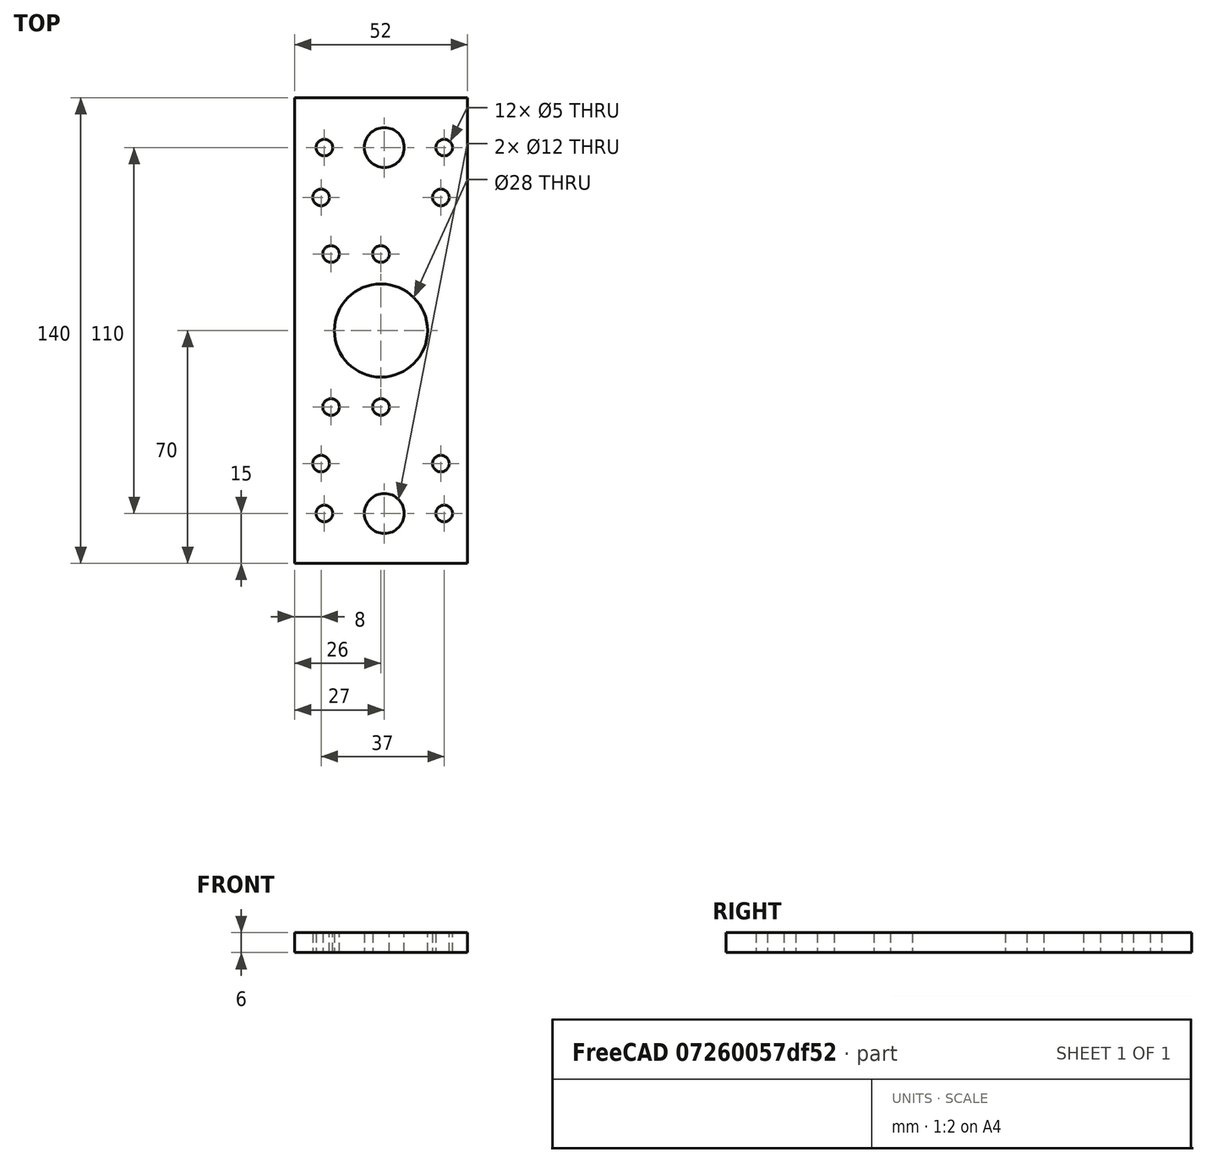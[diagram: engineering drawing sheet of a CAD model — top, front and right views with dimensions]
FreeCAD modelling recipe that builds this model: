
FCSTD DOCUMENT  (FreeCAD 0.15R4671 (Git))
Label: top
License: All rights reserved
LicenseURL: http://en.wikipedia.org/wiki/All_rights_reserved
objects: Drawing::FeatureView×25, Drawing::FeatureViewPart×2, Sketcher::SketchObject×1, PartDesign::Pad×1, Drawing::FeaturePage×1
note: 3 computed .brp shape members not serialized (recipe doc carries the construction recipe); baked Part::Feature solids carry a one-line shape summary decoded from their .brp

FEATURE [Sketcher::SketchObject] Sketch  label="top-sketch"
  sketch-geometry (32):
    g0: LineSegment StartX=-26 StartY=70 StartZ=0 EndX=26 EndY=70 EndZ=0
    g1: LineSegment StartX=26 StartY=70 StartZ=0 EndX=26 EndY=-70 EndZ=0
    g2: LineSegment StartX=26 StartY=-70 StartZ=0 EndX=-26 EndY=-70 EndZ=0
    g3: LineSegment StartX=-26 StartY=-70 StartZ=0 EndX=-26 EndY=70 EndZ=0
    g4: Circle CenterX=0 CenterY=0 CenterZ=0 NormalX=0 NormalY=0 NormalZ=1 Radius=14
    g5: LineSegment [constr] StartX=-15 StartY=23 StartZ=0 EndX=0 EndY=23 EndZ=0
    g6: LineSegment [constr] StartX=0 StartY=23 StartZ=0 EndX=0 EndY=-23 EndZ=0
    g7: LineSegment [constr] StartX=0 StartY=-23 StartZ=0 EndX=-15 EndY=-23 EndZ=0
    g8: LineSegment [constr] StartX=-15 StartY=-23 StartZ=0 EndX=-15 EndY=23 EndZ=0
    g9: Circle CenterX=-15 CenterY=23 CenterZ=0 NormalX=0 NormalY=0 NormalZ=1 Radius=2.5
    g10: Circle CenterX=0 CenterY=23 CenterZ=0 NormalX=0 NormalY=0 NormalZ=1 Radius=2.5
    g11: Circle CenterX=-15 CenterY=-23 CenterZ=0 NormalX=0 NormalY=0 NormalZ=1 Radius=2.5
    g12: Circle CenterX=0 CenterY=-23 CenterZ=0 NormalX=0 NormalY=0 NormalZ=1 Radius=2.5
    g13: LineSegment [constr] StartX=-18 StartY=40 StartZ=0 EndX=18 EndY=40 EndZ=0
    g14: LineSegment [constr] StartX=18 StartY=40 StartZ=0 EndX=18 EndY=-40 EndZ=0
    g15: LineSegment [constr] StartX=18 StartY=-40 StartZ=0 EndX=-18 EndY=-40 EndZ=0
    g16: LineSegment [constr] StartX=-18 StartY=-40 StartZ=0 EndX=-18 EndY=40 EndZ=0
    g17: Circle CenterX=-18 CenterY=40 CenterZ=0 NormalX=0 NormalY=0 NormalZ=1 Radius=2.5
    g18: Circle CenterX=18 CenterY=40 CenterZ=0 NormalX=0 NormalY=0 NormalZ=1 Radius=2.5
    g19: Circle CenterX=18 CenterY=-40 CenterZ=0 NormalX=0 NormalY=0 NormalZ=1 Radius=2.5
    g20: Circle CenterX=-18 CenterY=-40 CenterZ=0 NormalX=0 NormalY=0 NormalZ=1 Radius=2.5
    g21: LineSegment [constr] StartX=-17 StartY=55 StartZ=0 EndX=19 EndY=55 EndZ=0
    g22: LineSegment [constr] StartX=19 StartY=55 StartZ=0 EndX=19 EndY=-55 EndZ=0
    g23: LineSegment [constr] StartX=19 StartY=-55 StartZ=0 EndX=-17 EndY=-55 EndZ=0
    g24: LineSegment [constr] StartX=-17 StartY=-55 StartZ=0 EndX=-17 EndY=55 EndZ=0
    g25: Circle CenterX=1 CenterY=55 CenterZ=0 NormalX=0 NormalY=0 NormalZ=1 Radius=6
    g26: Circle CenterX=1 CenterY=-55 CenterZ=0 NormalX=0 NormalY=0 NormalZ=1 Radius=6
    g27: LineSegment [constr] StartX=1 StartY=55 StartZ=0 EndX=1 EndY=-55 EndZ=0
    g28: Circle CenterX=-17 CenterY=55 CenterZ=0 NormalX=0 NormalY=0 NormalZ=1 Radius=2.5
    g29: Circle CenterX=19 CenterY=55 CenterZ=0 NormalX=0 NormalY=0 NormalZ=1 Radius=2.5
    g30: Circle CenterX=-17 CenterY=-55 CenterZ=0 NormalX=0 NormalY=0 NormalZ=1 Radius=2.5
    g31: Circle CenterX=19 CenterY=-55 CenterZ=0 NormalX=0 NormalY=0 NormalZ=1 Radius=2.5
  constraints (82):
    c: Coincident(g1,g2)
    c: Coincident(g2,g3)
    c: Coincident(g3,g0)
    c: Horizontal(g0)
    c: Horizontal(g2)
    c: Vertical(g1)
    c: Vertical(g3)
    c: Symmetric(g1,g2,g-2)
    c: Symmetric(g0,g1,g-1)
    c: Coincident(g4,g-1)
    c: Radius(g4) = 14
    c: Coincident(g5,g6)
    c: Coincident(g6,g7)
    c: Coincident(g7,g8)
    c: Coincident(g8,g5)
    c: Horizontal(g5)
    c: Horizontal(g7)
    c: Vertical(g6)
    c: Vertical(g8)
    c: PointOnObject(g6,g-2)
    c: Symmetric(g5,g6,g-1)
    c: DistanceY(g5,g7) = -46
    c: DistanceX(g5,g5) = 15
    c: Coincident(g9,g5)
    c: Coincident(g10,g5)
    c: Coincident(g11,g7)
    c: Coincident(g12,g6)
    c: Radius(g12) = 2.5
    c: Equal(g12,g11)
    c: Equal(g12,g9)
    c: Equal(g12,g10)
    c: Coincident(g13,g14)
    c: Coincident(g14,g15)
    c: Coincident(g15,g16)
    c: Coincident(g16,g13)
    c: Horizontal(g13)
    c: Horizontal(g15)
    c: Vertical(g14)
    c: Vertical(g16)
    c: Symmetric(g13,g14,g-1)
    c: Symmetric(g14,g15,g-2)
    c: DistanceX(g15,g14) = 36
    c: DistanceY(g13,g15) = -80
    c: Coincident(g17,g13)
    c: Coincident(g18,g13)
    c: Coincident(g19,g14)
    c: Coincident(g20,g15)
    c: Radius(g17) = 2.5
    c: Equal(g17,g18)
    c: Equal(g17,g19)
    c: Equal(g17,g20)
    c: Coincident(g22,g23)
    c: Coincident(g23,g24)
    c: Coincident(g24,g21)
    c: Horizontal(g21)
    c: Horizontal(g23)
    c: Vertical(g22)
    c: Vertical(g24)
    c: PointOnObject(g25,g21)
    c: PointOnObject(g26,g23)
    c: Radius(g26) = 6
    c: Equal(g26,g25)
    c: Coincident(g27,g25)
    c: Coincident(g27,g26)
    c: Vertical(g27)
    c: Symmetric(g21,g23,g-1)
    c: Symmetric(g21,g21,g25)
    c: Coincident(g28,g21)
    c: Coincident(g30,g23)
    c: Coincident(g31,g22)
    c: Radius(g31) = 2.5
    c: Equal(g31,g30)
    c: Equal(g31,g29)
    c: Equal(g31,g28)
    c: DistanceY(g21,g23) = -110
    c: DistanceY(g21,g0) = 15
    c: Coincident(g21,g22)
    c: Coincident(g29,g21)
    c: DistanceX(g21,g21) = -36
    c: DistanceX(g21,g0) = 7
    c: DistanceX(g-1,g21) = 19
    c: Coincident(g1,g0)
FEATURE [PartDesign::Pad] Pad  label="top"
  Length = 6
  Length2 = 100
  Sketch = -> Sketch
  Type = 0
FEATURE [Drawing::FeatureViewPart] Ortho  label="Ortho_0_0"
  Direction = (1,0,0)
  HiddenWidth = 0.15
  LineWidth = 0.35
  Rotation = -90
  Scale = 1.5
  ShowHiddenLines = false
  ShowSmoothLines = false
  Source = -> Pad
  Tolerance = 0.05
  ViewResult = <g id="Ortho_0_0"\n   transform="rotate(-90,148.5,169) translate(148.5,169) scale(1.5,1.5)"\n  >\n<g   stroke="rgb(0, 0, 0)"\n   stroke-width="0.233333"\n   stroke-linecap="butt"\n   stroke-linejoin="miter"\n   fill="none"\n   transform="scale(1,-1)"\n  >\n<path id= "1" d=" M 0 -70 L 6 -70 " />\n<path id= "2" d=" M 0 70 L 6 70 " />\n<path id= "3" d=" M 0 -70 L 0 70 " />\n<path id= "4" d=" M 6 -70 L 6 70 " />\n</g>\n</g>
  Visible = true
  X = 148.5
  Y = 169
FEATURE [Drawing::FeatureViewPart] Ortho001  label="Ortho_0_1"
  Direction = (0,0,1)
  HiddenWidth = 0.15
  LineWidth = 0.35
  Rotation = 90
  Scale = 1.5
  ShowHiddenLines = false
  ShowSmoothLines = false
  Source = -> Pad
  Tolerance = 0.05
  ViewResult = <g id="Ortho_0_1"\n   transform="rotate(90,148.5,80) translate(148.5,80) scale(1.5,1.5)"\n  >\n<g   stroke="rgb(0, 0, 0)"\n   stroke-width="0.233333"\n   stroke-linecap="butt"\n   stroke-linejoin="miter"\n   fill="none"\n   transform="scale(1,-1)"\n  >\n<path id= "1" d=" M -26 70 L 26 70 " />\n<path id= "2" d=" M 26 70 L 26 -70 " />\n<path id= "3" d=" M 26 -70 L -26 -70 " />\n<path id= "4" d=" M -26 -70 L -26 70 " />\n<circle cx ="0" cy ="0" r ="14" /><circle cx ="1" cy ="-55" r ="6" /><circle cx ="1" cy ="55" r ="6" /><circle cx ="19" cy ="-55" r ="2.5" /><circle cx ="-17" cy ="-55" r ="2.5" /><circle cx ="19" cy ="55" r ="2.5" /><circle cx ="-17" cy ="55" r ="2.5" /><circle cx ="-18" cy ="-40" r ="2.5" /><circle cx ="18" cy ="-40" r ="2.5" /><circle cx ="18" cy ="40" r ="2.5" /><circle cx ="-18" cy ="40" r ="2.5" /><circle cx ="0" cy ="-23" r ="2.5" /><circle cx ="0" cy ="23" r ="2.5" /><circle cx ="-15" cy ="-23" r ="2.5" /><circle cx ="-15" cy ="23" r ="2.5" /></g>\n</g>
  Visible = true
  X = 148.5
  Y = 80
FEATURE [Drawing::FeatureView] centerLines001
  Rotation = 0
  ViewResult = <g transform="scale(1.500000,1.500000)" stroke="rgb(0,0,255)"  stroke-width="0.213333" > <path d="M 99.000000,53.333333 L 99.000000,51.333333 M 99.000000,50.000000 L 99.000000,46.000000 M 99.000000,44.666667 L 99.000000,42.666667 M 99.000000,41.333333 L 99.000000,37.333333 M 99.000000,36.000000 L 99.000000,34.000000 M 99.000000,32.666667 L 99.000000,28.666667 M 99.000000,27.333333 L 99.000000,26.488089 "/>\n<path d="M 99.000000,53.333333 L 97.000000,53.333333 M 95.666667,53.333333 L 91.666667,53.333333 M 90.333333,53.333333 L 88.333333,53.333333 M 87.000000,53.333333 L 83.000000,53.333333 M 81.666667,53.333333 L 79.666667,53.333333 M 78.333333,53.333333 L 74.333333,53.333333 M 73.000000,53.333333 L 71.000000,53.333333 "/>\n<path d="M 99.000000,53.333333 L 99.000000,55.333333 M 99.000000,56.666667 L 99.000000,60.666667 M 99.000000,62.000000 L 99.000000,64.000000 M 99.000000,65.333333 L 99.000000,69.333333 M 99.000000,70.666667 L 99.000000,72.666667 M 99.000000,74.000000 L 99.000000,78.000000 M 99.000000,79.333333 L 99.000000,81.333333 M 99.000000,82.666667 L 99.000000,82.745978 "/>\n<path d="M 99.000000,53.333333 L 101.000000,53.333333 M 102.333333,53.333333 L 106.333333,53.333333 M 107.666667,53.333333 L 109.666667,53.333333 M 111.000000,53.333333 L 115.000000,53.333333 M 116.333333,53.333333 L 118.333333,53.333333 M 119.666667,53.333333 L 123.666667,53.333333 M 125.000000,53.333333 L 127.000000,53.333333 "/> </g> 
  Visible = true
  X = 0
  Y = 0
FEATURE [Drawing::FeatureView] dimStack001
  Rotation = 0
  ViewResult = <g> <line x1="111.999999" y1="80.000000" x2="102.514823" y2="80.000000" style="stroke:rgb(0,0,255);stroke-width:0.50" />\n<line x1="251.499999" y1="119.000000" x2="102.514823" y2="119.000000" style="stroke:rgb(0,0,255);stroke-width:0.50" />\n<line x1="103.514823" y1="80.000000" x2="103.514823" y2="119.000000" style="stroke:rgb(0,0,255);stroke-width:0.50" />\n<polygon points="103.514823,80.000000 102.514823,83.000000 103.514823,84.000000 104.514823,83.000000" style="fill:rgb(0,0,255);stroke:rgb(0,0,255);stroke-width:0" />\n<polygon points="103.514823,119.000000 104.514823,116.000000 103.514823,115.000000 102.514823,116.000000" style="fill:rgb(0,0,255);stroke:rgb(0,0,255);stroke-width:0" />\n<text x="101.514823" y="99.500000" font-family="inherit" font-size="3.6" fill="rgb(0,0,255)" text-anchor="middle" transform="rotate(-90.000000 101.514823,99.500000)" >26</text> </g> 
  Visible = true
  X = 0
  Y = 0
FEATURE [Drawing::FeatureView] dimStack002
  Rotation = 0
  ViewResult = <g> <line x1="111.999999" y1="57.500000" x2="102.494799" y2="57.500000" style="stroke:rgb(0,0,255);stroke-width:0.50" />\n<line x1="111.999999" y1="80.000000" x2="102.494799" y2="80.000000" style="stroke:rgb(0,0,255);stroke-width:0.50" />\n<line x1="103.494799" y1="57.500000" x2="103.494799" y2="80.000000" style="stroke:rgb(0,0,255);stroke-width:0.50" />\n<polygon points="103.494799,57.500000 102.494799,60.500000 103.494799,61.500000 104.494799,60.500000" style="fill:rgb(0,0,255);stroke:rgb(0,0,255);stroke-width:0" />\n<polygon points="103.494799,80.000000 104.494799,77.000000 103.494799,76.000000 102.494799,77.000000" style="fill:rgb(0,0,255);stroke:rgb(0,0,255);stroke-width:0" />\n<text x="101.494799" y="68.750000" font-family="inherit" font-size="3.6" fill="rgb(0,0,255)" text-anchor="middle" transform="rotate(-90.000000 101.494799,68.750000)" >15</text> </g> 
  Visible = true
  X = 0
  Y = 0
FEATURE [Drawing::FeatureView] dim002
  Rotation = 0
  ViewResult = <g> \n  <line x1="114.000000" y1="55.500000" x2="114.000000" y2="32.992271" style="stroke:rgb(0,0,255);stroke-width:0.50" />\n<line x1="183.000000" y1="55.500000" x2="183.000000" y2="32.992271" style="stroke:rgb(0,0,255);stroke-width:0.50" />\n<line x1="114.000000" y1="33.992271" x2="183.000000" y2="33.992271" style="stroke:rgb(0,0,255);stroke-width:0.50" /> \n  <polygon points="183.000000,33.992271 180.000000,32.992271 179.000000,33.992271 180.000000,34.992271" style="fill:rgb(0,0,255);stroke:rgb(0,0,255);stroke-width:0" /><polygon points="114.000000,33.992271 117.000000,34.992271 118.000000,33.992271 117.000000,32.992271" style="fill:rgb(0,0,255);stroke:rgb(0,0,255);stroke-width:0" /> \n  <text x="148.500000" y="31.992271" font-family="inherit" font-size="3.6" fill="rgb(0,0,255)" text-anchor="middle" transform="rotate(0.000000 148.500000,31.992271)" >46</text> </g>
  Visible = true
  X = 0
  Y = 0
FEATURE [Drawing::FeatureView] dim003
  Rotation = 0
  ViewResult = <g> \n  <line x1="88.500000" y1="51.000000" x2="88.500000" y2="25.019274" style="stroke:rgb(0,0,255);stroke-width:0.50" />\n<line x1="208.500000" y1="51.000000" x2="208.500000" y2="25.019274" style="stroke:rgb(0,0,255);stroke-width:0.50" />\n<line x1="88.500000" y1="26.019274" x2="208.500000" y2="26.019274" style="stroke:rgb(0,0,255);stroke-width:0.50" /> \n  <polygon points="208.500000,26.019274 205.500000,25.019274 204.500000,26.019274 205.500000,27.019274" style="fill:rgb(0,0,255);stroke:rgb(0,0,255);stroke-width:0" /><polygon points="88.500000,26.019274 91.500000,27.019274 92.500000,26.019274 91.500000,25.019274" style="fill:rgb(0,0,255);stroke:rgb(0,0,255);stroke-width:0" /> \n  <text x="148.500000" y="24.019274" font-family="inherit" font-size="3.6" fill="rgb(0,0,255)" text-anchor="middle" transform="rotate(0.000000 148.500000,24.019274)" >80</text> </g>
  Visible = true
  X = 0
  Y = 0
FEATURE [Drawing::FeatureView] dim004
  Rotation = 0
  ViewResult = <g> \n  <line x1="66.000000" y1="52.500000" x2="66.000000" y2="15.562372" style="stroke:rgb(0,0,255);stroke-width:0.50" />\n<line x1="231.000000" y1="52.500000" x2="231.000000" y2="15.562372" style="stroke:rgb(0,0,255);stroke-width:0.50" />\n<line x1="66.000000" y1="16.562372" x2="231.000000" y2="16.562372" style="stroke:rgb(0,0,255);stroke-width:0.50" /> \n  <polygon points="231.000000,16.562372 228.000000,15.562372 227.000000,16.562372 228.000000,17.562372" style="fill:rgb(0,0,255);stroke:rgb(0,0,255);stroke-width:0" /><polygon points="66.000000,16.562372 69.000000,17.562372 70.000000,16.562372 69.000000,15.562372" style="fill:rgb(0,0,255);stroke:rgb(0,0,255);stroke-width:0" /> \n  <text x="148.500000" y="14.562372" font-family="inherit" font-size="3.6" fill="rgb(0,0,255)" text-anchor="middle" transform="rotate(0.000000 148.500000,14.562372)" >110</text> </g>
  Visible = true
  X = 0
  Y = 0
FEATURE [Drawing::FeatureView] centerLines002
  Rotation = 0
  ViewResult = <g transform="scale(1.500000,1.500000)" stroke="rgb(0,0,255)"  stroke-width="0.213333" > <path d="M 44.000000,54.333333 L 44.000000,52.333333 M 44.000000,51.000000 L 44.000000,47.000000 M 44.000000,45.666667 L 44.000000,43.666667 M 44.000000,42.333333 L 44.000000,38.333333 M 44.000000,37.000000 L 44.000000,35.000000 M 44.000000,33.666667 L 44.000000,29.666667 M 44.000000,28.333333 L 44.000000,28.031921 "/>\n<path d="M 44.000000,54.333333 L 42.000000,54.333333 M 40.666667,54.333333 L 36.805270,54.333333 "/>\n<path d="M 44.000000,54.333333 L 44.000000,56.333333 M 44.000000,57.666667 L 44.000000,61.666667 M 44.000000,63.000000 L 44.000000,65.000000 M 44.000000,66.333333 L 44.000000,70.333333 M 44.000000,71.666667 L 44.000000,73.666667 M 44.000000,75.000000 L 44.000000,75.964366 "/>\n<path d="M 44.000000,54.333333 L 46.000000,54.333333 M 47.333333,54.333333 L 51.333333,54.333333 "/> </g> 
  Visible = true
  X = 0
  Y = 0
FEATURE [Drawing::FeatureView] centerLines003
  Rotation = 0
  ViewResult = <g transform="scale(1.500000,1.500000)" stroke="rgb(0,0,255)"  stroke-width="0.213333" > <path d="M 154.000000,54.333333 L 154.000000,52.333333 M 154.000000,51.000000 L 154.000000,47.000000 M 154.000000,45.666667 L 154.000000,43.666667 M 154.000000,42.333333 L 154.000000,38.333333 M 154.000000,37.000000 L 154.000000,35.000000 M 154.000000,33.666667 L 154.000000,32.739572 "/>\n<path d="M 154.000000,54.333333 L 152.000000,54.333333 M 150.666667,54.333333 L 146.666667,54.333333 "/>\n<path d="M 154.000000,54.333333 L 154.000000,56.333333 M 154.000000,57.666667 L 154.000000,61.666667 M 154.000000,63.000000 L 154.000000,65.000000 M 154.000000,66.333333 L 154.000000,70.333333 M 154.000000,71.666667 L 154.000000,73.666667 M 154.000000,75.000000 L 154.000000,75.536398 "/>\n<path d="M 154.000000,54.333333 L 156.000000,54.333333 M 157.333333,54.333333 L 161.333333,54.333333 M 162.666667,54.333333 L 164.339812,54.333333 "/> </g> 
  Visible = true
  X = 0
  Y = 0
FEATURE [Drawing::FeatureView] dim001
  Rotation = 0
  ViewResult = <g> \n  <line x1="43.500000" y1="121.000000" x2="43.500000" y2="128.238828" style="stroke:rgb(0,0,255);stroke-width:0.50" />\n<line x1="66.000000" y1="110.500000" x2="66.000000" y2="128.238828" style="stroke:rgb(0,0,255);stroke-width:0.50" />\n<line x1="43.500000" y1="127.238828" x2="66.000000" y2="127.238828" style="stroke:rgb(0,0,255);stroke-width:0.50" /> \n  <polygon points="66.000000,127.238828 63.000000,126.238828 62.000000,127.238828 63.000000,128.238828" style="fill:rgb(0,0,255);stroke:rgb(0,0,255);stroke-width:0" /><polygon points="43.500000,127.238828 46.500000,128.238828 47.500000,127.238828 46.500000,126.238828" style="fill:rgb(0,0,255);stroke:rgb(0,0,255);stroke-width:0" /> \n  <text x="54.750000" y="125.238828" font-family="inherit" font-size="3.6" fill="rgb(0,0,255)" text-anchor="middle" transform="rotate(0.000000 54.750000,125.238828)" >15</text> </g>
  Visible = true
  X = 0
  Y = 0
FEATURE [Drawing::FeatureView] dim005
  Rotation = 0
  ViewResult = <g> \n  <line x1="43.500000" y1="121.000000" x2="43.500000" y2="137.154833" style="stroke:rgb(0,0,255);stroke-width:0.50" />\n<line x1="88.500000" y1="109.000000" x2="88.500000" y2="137.154833" style="stroke:rgb(0,0,255);stroke-width:0.50" />\n<line x1="43.500000" y1="136.154833" x2="88.500000" y2="136.154833" style="stroke:rgb(0,0,255);stroke-width:0.50" /> \n  <polygon points="88.500000,136.154833 85.500000,135.154833 84.500000,136.154833 85.500000,137.154833" style="fill:rgb(0,0,255);stroke:rgb(0,0,255);stroke-width:0" /><polygon points="43.500000,136.154833 46.500000,137.154833 47.500000,136.154833 46.500000,135.154833" style="fill:rgb(0,0,255);stroke:rgb(0,0,255);stroke-width:0" /> \n  <text x="66.000000" y="134.154833" font-family="inherit" font-size="3.6" fill="rgb(0,0,255)" text-anchor="middle" transform="rotate(0.000000 66.000000,134.154833)" >30</text> </g>
  Visible = true
  X = 0
  Y = 0
FEATURE [Drawing::FeatureView] dim006
  Rotation = 0
  ViewResult = <g> \n  <line x1="43.500000" y1="121.000000" x2="43.500000" y2="145.699338" style="stroke:rgb(0,0,255);stroke-width:0.50" />\n<line x1="114.000000" y1="82.000000" x2="114.000000" y2="145.699338" style="stroke:rgb(0,0,255);stroke-width:0.50" />\n<line x1="43.500000" y1="144.699338" x2="114.000000" y2="144.699338" style="stroke:rgb(0,0,255);stroke-width:0.50" /> \n  <polygon points="114.000000,144.699338 111.000000,143.699338 110.000000,144.699338 111.000000,145.699338" style="fill:rgb(0,0,255);stroke:rgb(0,0,255);stroke-width:0" /><polygon points="43.500000,144.699338 46.500000,145.699338 47.500000,144.699338 46.500000,143.699338" style="fill:rgb(0,0,255);stroke:rgb(0,0,255);stroke-width:0" /> \n  <text x="78.750000" y="142.699338" font-family="inherit" font-size="3.6" fill="rgb(0,0,255)" text-anchor="middle" transform="rotate(0.000000 78.750000,142.699338)" >47</text> </g>
  Visible = true
  X = 0
  Y = 0
FEATURE [Drawing::FeatureView] dim007
  Rotation = 0
  ViewResult = <g> \n  <line x1="43.500000" y1="121.000000" x2="43.500000" y2="154.429593" style="stroke:rgb(0,0,255);stroke-width:0.50" />\n<line x1="148.500000" y1="126.118967" x2="148.500000" y2="154.429593" style="stroke:rgb(0,0,255);stroke-width:0.50" />\n<line x1="43.500000" y1="153.429593" x2="148.500000" y2="153.429593" style="stroke:rgb(0,0,255);stroke-width:0.50" /> \n  <polygon points="148.500000,153.429593 145.500000,152.429593 144.500000,153.429593 145.500000,154.429593" style="fill:rgb(0,0,255);stroke:rgb(0,0,255);stroke-width:0" /><polygon points="43.500000,153.429593 46.500000,154.429593 47.500000,153.429593 46.500000,152.429593" style="fill:rgb(0,0,255);stroke:rgb(0,0,255);stroke-width:0" /> \n  <text x="96.000000" y="151.429593" font-family="inherit" font-size="3.6" fill="rgb(0,0,255)" text-anchor="middle" transform="rotate(0.000000 96.000000,151.429593)" >70</text> </g>
  Visible = true
  X = 0
  Y = 0
FEATURE [Drawing::FeatureView] dim009
  Rotation = 0
  ViewResult = <g> \n  <line x1="86.500000" y1="107.000000" x2="82.132835" y2="107.000000" style="stroke:rgb(0,0,255);stroke-width:0.50" />\n<line x1="86.500000" y1="53.000000" x2="82.132835" y2="53.000000" style="stroke:rgb(0,0,255);stroke-width:0.50" />\n<line x1="83.132835" y1="107.000000" x2="83.132835" y2="53.000000" style="stroke:rgb(0,0,255);stroke-width:0.50" /> \n  <polygon points="83.132835,53.000000 82.132835,56.000000 83.132835,57.000000 84.132835,56.000000" style="fill:rgb(0,0,255);stroke:rgb(0,0,255);stroke-width:0" /><polygon points="83.132835,107.000000 84.132835,104.000000 83.132835,103.000000 82.132835,104.000000" style="fill:rgb(0,0,255);stroke:rgb(0,0,255);stroke-width:0" /> \n  <text x="81.132835" y="80.000000" font-family="inherit" font-size="3.6" fill="rgb(0,0,255)" text-anchor="middle" transform="rotate(-90.000000 81.132835,80.000000)" >36</text> </g>
  Visible = true
  X = 0
  Y = 0
FEATURE [Drawing::FeatureView] dim008
  Rotation = 0
  ViewResult = <g> \n  <line x1="86.500000" y1="107.000000" x2="82.200572" y2="107.000000" style="stroke:rgb(0,0,255);stroke-width:0.50" />\n<line x1="251.500000" y1="119.000000" x2="82.200572" y2="119.000000" style="stroke:rgb(0,0,255);stroke-width:0.50" />\n<line x1="83.200572" y1="107.000000" x2="83.200572" y2="119.000000" style="stroke:rgb(0,0,255);stroke-width:0.50" /> \n  <polygon points="83.200572,119.000000 84.200572,116.000000 83.200572,115.000000 82.200572,116.000000" style="fill:rgb(0,0,255);stroke:rgb(0,0,255);stroke-width:0" /><polygon points="83.200572,107.000000 82.200572,110.000000 83.200572,111.000000 84.200572,110.000000" style="fill:rgb(0,0,255);stroke:rgb(0,0,255);stroke-width:0" /> \n  <text x="81.200572" y="113.000000" font-family="inherit" font-size="3.6" fill="rgb(0,0,255)" text-anchor="middle" transform="rotate(-90.000000 81.200572,113.000000)" >8</text> </g>
  Visible = true
  X = 0
  Y = 0
FEATURE [Drawing::FeatureView] dim013
  Rotation = 0
  ViewResult = <g> \n  <line x1="43.500000" y1="39.000000" x2="43.500000" y2="7.087072" style="stroke:rgb(0,0,255);stroke-width:0.50" />\n<line x1="253.500000" y1="39.000000" x2="253.500000" y2="7.087072" style="stroke:rgb(0,0,255);stroke-width:0.50" />\n<line x1="43.500000" y1="8.087072" x2="253.500000" y2="8.087072" style="stroke:rgb(0,0,255);stroke-width:0.50" /> \n  <polygon points="253.500000,8.087072 250.500000,7.087072 249.500000,8.087072 250.500000,9.087072" style="fill:rgb(0,0,255);stroke:rgb(0,0,255);stroke-width:0" /><polygon points="43.500000,8.087072 46.500000,9.087072 47.500000,8.087072 46.500000,7.087072" style="fill:rgb(0,0,255);stroke:rgb(0,0,255);stroke-width:0" /> \n  <text x="148.500000" y="6.087072" font-family="inherit" font-size="3.6" fill="rgb(0,0,255)" text-anchor="middle" transform="rotate(0.000000 148.500000,6.087072)" >140</text> </g>
  Visible = true
  X = 0
  Y = 0
FEATURE [Drawing::FeatureView] dim010
  Rotation = 0
  ViewResult = <g> \n  <line x1="64.000000" y1="81.500000" x2="35.626230" y2="81.500000" style="stroke:rgb(0,0,255);stroke-width:0.50" />\n<line x1="64.000000" y1="108.500000" x2="35.626230" y2="108.500000" style="stroke:rgb(0,0,255);stroke-width:0.50" />\n<line x1="36.626230" y1="81.500000" x2="36.626230" y2="108.500000" style="stroke:rgb(0,0,255);stroke-width:0.50" /> \n  <polygon points="36.626230,108.500000 37.626230,105.500000 36.626230,104.500000 35.626230,105.500000" style="fill:rgb(0,0,255);stroke:rgb(0,0,255);stroke-width:0" /><polygon points="36.626230,81.500000 35.626230,84.500000 36.626230,85.500000 37.626230,84.500000" style="fill:rgb(0,0,255);stroke:rgb(0,0,255);stroke-width:0" /> \n  <text x="34.626230" y="95.000000" font-family="inherit" font-size="3.6" fill="rgb(0,0,255)" text-anchor="middle" transform="rotate(-90.000000 34.626230,95.000000)" >18</text> </g>
  Visible = true
  X = 0
  Y = 0
FEATURE [Drawing::FeatureView] dim011
  Rotation = 0
  ViewResult = <g> \n  <line x1="64.000000" y1="108.500000" x2="35.634050" y2="108.500000" style="stroke:rgb(0,0,255);stroke-width:0.50" />\n<line x1="41.500000" y1="119.000000" x2="35.634050" y2="119.000000" style="stroke:rgb(0,0,255);stroke-width:0.50" />\n<line x1="36.634050" y1="108.500000" x2="36.634050" y2="119.000000" style="stroke:rgb(0,0,255);stroke-width:0.50" /> \n  <polygon points="36.634050,119.000000 37.634050,116.000000 36.634050,115.000000 35.634050,116.000000" style="fill:rgb(0,0,255);stroke:rgb(0,0,255);stroke-width:0" /><polygon points="36.634050,108.500000 35.634050,111.500000 36.634050,112.500000 37.634050,111.500000" style="fill:rgb(0,0,255);stroke:rgb(0,0,255);stroke-width:0" /> \n  <text x="34.634050" y="113.750000" font-family="inherit" font-size="3.6" fill="rgb(0,0,255)" text-anchor="middle" transform="rotate(-90.000000 34.634050,113.750000)" >7</text> </g>
  Visible = true
  X = 0
  Y = 0
FEATURE [Drawing::FeatureView] dim012
  Rotation = 0
  ViewResult = <g> \n  <line x1="64.000000" y1="108.500000" x2="26.550457" y2="108.500000" style="stroke:rgb(0,0,255);stroke-width:0.50" />\n<line x1="64.000000" y1="54.500000" x2="26.550457" y2="54.500000" style="stroke:rgb(0,0,255);stroke-width:0.50" />\n<line x1="27.550457" y1="108.500000" x2="27.550457" y2="54.500000" style="stroke:rgb(0,0,255);stroke-width:0.50" /> \n  <polygon points="27.550457,54.500000 26.550457,57.500000 27.550457,58.500000 28.550457,57.500000" style="fill:rgb(0,0,255);stroke:rgb(0,0,255);stroke-width:0" /><polygon points="27.550457,108.500000 28.550457,105.500000 27.550457,104.500000 26.550457,105.500000" style="fill:rgb(0,0,255);stroke:rgb(0,0,255);stroke-width:0" /> \n  <text x="25.550457" y="81.500000" font-family="inherit" font-size="3.6" fill="rgb(0,0,255)" text-anchor="middle" transform="rotate(-90.000000 25.550457,81.500000)" >36</text> </g>
  Visible = true
  X = 0
  Y = 0
FEATURE [Drawing::FeatureView] dim014
  Rotation = 0
  ViewResult = <g> \n  <line x1="41.500000" y1="41.000000" x2="15.525755" y2="41.000000" style="stroke:rgb(0,0,255);stroke-width:0.50" />\n<line x1="41.500000" y1="119.000000" x2="15.525755" y2="119.000000" style="stroke:rgb(0,0,255);stroke-width:0.50" />\n<line x1="16.525755" y1="41.000000" x2="16.525755" y2="119.000000" style="stroke:rgb(0,0,255);stroke-width:0.50" /> \n  <polygon points="16.525755,119.000000 17.525755,116.000000 16.525755,115.000000 15.525755,116.000000" style="fill:rgb(0,0,255);stroke:rgb(0,0,255);stroke-width:0" /><polygon points="16.525755,41.000000 15.525755,44.000000 16.525755,45.000000 17.525755,44.000000" style="fill:rgb(0,0,255);stroke:rgb(0,0,255);stroke-width:0" /> \n  <text x="14.525755" y="80.000000" font-family="inherit" font-size="3.6" fill="rgb(0,0,255)" text-anchor="middle" transform="rotate(-90.000000 14.525755,80.000000)" >52</text> </g>
  Visible = true
  X = 0
  Y = 0
FEATURE [Drawing::FeatureView] dim015
  Rotation = 0
  ViewResult = <g> \n  <line x1="41.500000" y1="160.000000" x2="30.996674" y2="160.000000" style="stroke:rgb(0,0,255);stroke-width:0.50" />\n<line x1="41.500000" y1="169.000000" x2="30.996674" y2="169.000000" style="stroke:rgb(0,0,255);stroke-width:0.50" />\n<line x1="31.996674" y1="160.000000" x2="31.996674" y2="169.000000" style="stroke:rgb(0,0,255);stroke-width:0.50" /> \n  <polygon points="31.996674,169.000000 30.996674,172.000000 31.996674,173.000000 32.996674,172.000000" style="fill:rgb(0,0,255);stroke:rgb(0,0,255);stroke-width:0" /><polygon points="31.996674,160.000000 32.996674,157.000000 31.996674,156.000000 30.996674,157.000000" style="fill:rgb(0,0,255);stroke:rgb(0,0,255);stroke-width:0" /> \n  <text x="29.996674" y="164.500000" font-family="inherit" font-size="3.6" fill="rgb(0,0,255)" text-anchor="middle" transform="rotate(-90.000000 29.996674,164.500000)" >6</text> </g>
  Visible = true
  X = 0
  Y = 0
FEATURE [Drawing::FeatureView] dim016
  Rotation = 0
  ViewResult = <g>  <circle cx ="66.000000" cy ="81.500000" r="0.250000" stroke="none" fill="rgb(0,0,255)" /> \n<line x1="47.256627" y1="67.087532" x2="73.134630" y2="86.986079" style="stroke:rgb(0,0,255);stroke-width:0.50" />\n<polygon points="58.865370,76.013921 60.634016,78.635351 62.036317,78.452179 61.853144,77.049878" style="fill:rgb(0,0,255);stroke:rgb(0,0,255);stroke-width:0" />\n<polygon points="73.134630,86.986079 71.365984,84.364649 69.963683,84.547821 70.146856,85.950122" style="fill:rgb(0,0,255);stroke:rgb(0,0,255);stroke-width:0" />\n<line x1="47.256627" y1="67.087532" x2="62.024322" y2="67.087532" style="stroke:rgb(0,0,255);stroke-width:0.50" />\n<text x="54.640475" y="65.087532" font-family="inherit" font-size="3.6" fill="rgb(0,0,255)" text-anchor="middle"  >2 x Ø12</text> </g>
  Visible = true
  X = 0
  Y = 0
FEATURE [Drawing::FeatureView] dim017
  Rotation = 0
  ViewResult = <g>  <circle cx ="148.500000" cy ="80.000000" r="0.250000" stroke="none" fill="rgb(0,0,255)" /> \n<line x1="156.115642" y1="54.429507" x2="142.505788" y2="100.126336" style="stroke:rgb(0,0,255);stroke-width:0.50" />\n<polygon points="154.494212,59.873664 152.679499,62.463416 153.352458,63.707251 154.596293,63.034293" style="fill:rgb(0,0,255);stroke:rgb(0,0,255);stroke-width:0" />\n<polygon points="142.505788,100.126336 144.320501,97.536584 143.647542,96.292749 142.403707,96.965707" style="fill:rgb(0,0,255);stroke:rgb(0,0,255);stroke-width:0" />\n<line x1="156.115642" y1="54.429507" x2="175.102679" y2="54.429507" style="stroke:rgb(0,0,255);stroke-width:0.50" />\n<text x="165.609160" y="52.429507" font-family="inherit" font-size="3.6" fill="rgb(0,0,255)" text-anchor="middle" transform="rotate(0.000000 165.609160,52.429507)" >Ø28</text> </g>
  Visible = true
  X = 0
  Y = 0
FEATURE [Drawing::FeatureView] dim018
  Rotation = 0
  ViewResult = <g>  <circle cx ="66.000000" cy ="54.500000" r="0.250000" stroke="none" fill="rgb(0,0,255)" /> \n<line x1="69.619137" y1="48.522429" x2="64.057795" y2="57.707856" style="stroke:rgb(0,0,255);stroke-width:0.50" />\n<polygon points="67.942205,51.292144 70.351398,49.243781 70.013891,47.870432 68.640542,48.207938" style="fill:rgb(0,0,255);stroke:rgb(0,0,255);stroke-width:0" />\n<polygon points="64.057795,57.707856 61.648602,59.756219 61.986109,61.129568 63.359458,60.792062" style="fill:rgb(0,0,255);stroke:rgb(0,0,255);stroke-width:0" />\n<line x1="69.619137" y1="48.522429" x2="80.589426" y2="48.522429" style="stroke:rgb(0,0,255);stroke-width:0.50" />\n<text x="75.104282" y="46.522429" font-family="inherit" font-size="3.6" fill="rgb(0,0,255)" text-anchor="middle"  >4 x Ø5</text> </g>
  Visible = true
  X = 0
  Y = 0
FEATURE [Drawing::FeatureView] dim019
  Rotation = 0
  ViewResult = <g>  <circle cx ="88.500000" cy ="53.000000" r="0.250000" stroke="none" fill="rgb(0,0,255)" /> \n<line x1="91.559714" y1="47.678561" x2="86.630785" y2="56.250929" style="stroke:rgb(0,0,255);stroke-width:0.50" />\n<polygon points="90.369215,49.749071 92.731501,47.646786 92.363044,46.281414 90.997672,46.649871" style="fill:rgb(0,0,255);stroke:rgb(0,0,255);stroke-width:0" />\n<polygon points="86.630785,56.250929 84.268499,58.353214 84.636956,59.718586 86.002328,59.350129" style="fill:rgb(0,0,255);stroke:rgb(0,0,255);stroke-width:0" />\n<line x1="91.559714" y1="47.678561" x2="107.593212" y2="47.678561" style="stroke:rgb(0,0,255);stroke-width:0.50" />\n<text x="99.576463" y="45.678561" font-family="inherit" font-size="3.6" fill="rgb(0,0,255)" text-anchor="middle"  >4 x Ø5</text> </g>
  Visible = true
  X = 0
  Y = 0
FEATURE [Drawing::FeatureView] dim020
  Rotation = 0
  ViewResult = <g>  <circle cx ="114.000000" cy ="57.500000" r="0.250000" stroke="none" fill="rgb(0,0,255)" /> \n<line x1="118.563501" y1="48.522429" x2="112.300729" y2="60.842900" style="stroke:rgb(0,0,255);stroke-width:0.50" />\n<polygon points="115.699271,54.157100 117.950128,51.935920 117.511827,50.591341 116.167248,51.029642" style="fill:rgb(0,0,255);stroke:rgb(0,0,255);stroke-width:0" />\n<polygon points="112.300729,60.842900 110.049872,63.064080 110.488173,64.408659 111.832752,63.970358" style="fill:rgb(0,0,255);stroke:rgb(0,0,255);stroke-width:0" />\n<line x1="118.563501" y1="48.522429" x2="134.175065" y2="48.522429" style="stroke:rgb(0,0,255);stroke-width:0.50" />\n<text x="126.369283" y="46.522429" font-family="inherit" font-size="3.6" fill="rgb(0,0,255)" text-anchor="middle"  >4 x Ø5</text> </g>
  Visible = true
  X = 0
  Y = 0
FEATURE [Drawing::FeaturePage] Page001
  Group = -> [Ortho,Ortho001,centerLines001,dimStack001,dimStack002,dim002,dim003,dim004,centerLines002,centerLines003,dim001,dim005,dim006,dim007,dim009,dim008,dim013,dim010,dim011,dim012,dim014,dim015,dim016,dim017,dim018,dim019,dim020]
  Template = <path>
note: 1 file-system path scrubbed to <path> (originals preserved in the JSON sidecar)
